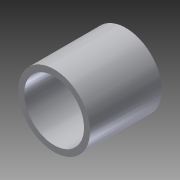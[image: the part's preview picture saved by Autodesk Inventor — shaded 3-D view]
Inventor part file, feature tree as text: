
AUTODESK INVENTOR PART (.ipt)
format: ipt  version: 2013 (Build 170138000, 138)  size: 86,528 bytes
history: native  units: in
note: dims shown in document units (in); Inventor stores cm internally (conversion verified against a paired STEP export)
features: extrude x1, sketch x1
ambient origin geometry x8: Origin, YZ Plane, XZ Plane, XY Plane, X Axis, Y Axis, Z Axis, Center Point
bodies: Solid1 (feature_tree)
feature tree (2):
  extrude  "Extrusion1"  Depth=0.625in
  sketch  "Sketch1"  dims[d0=0.75in d1=0.625in d2=0.75in d3=0.0in]
